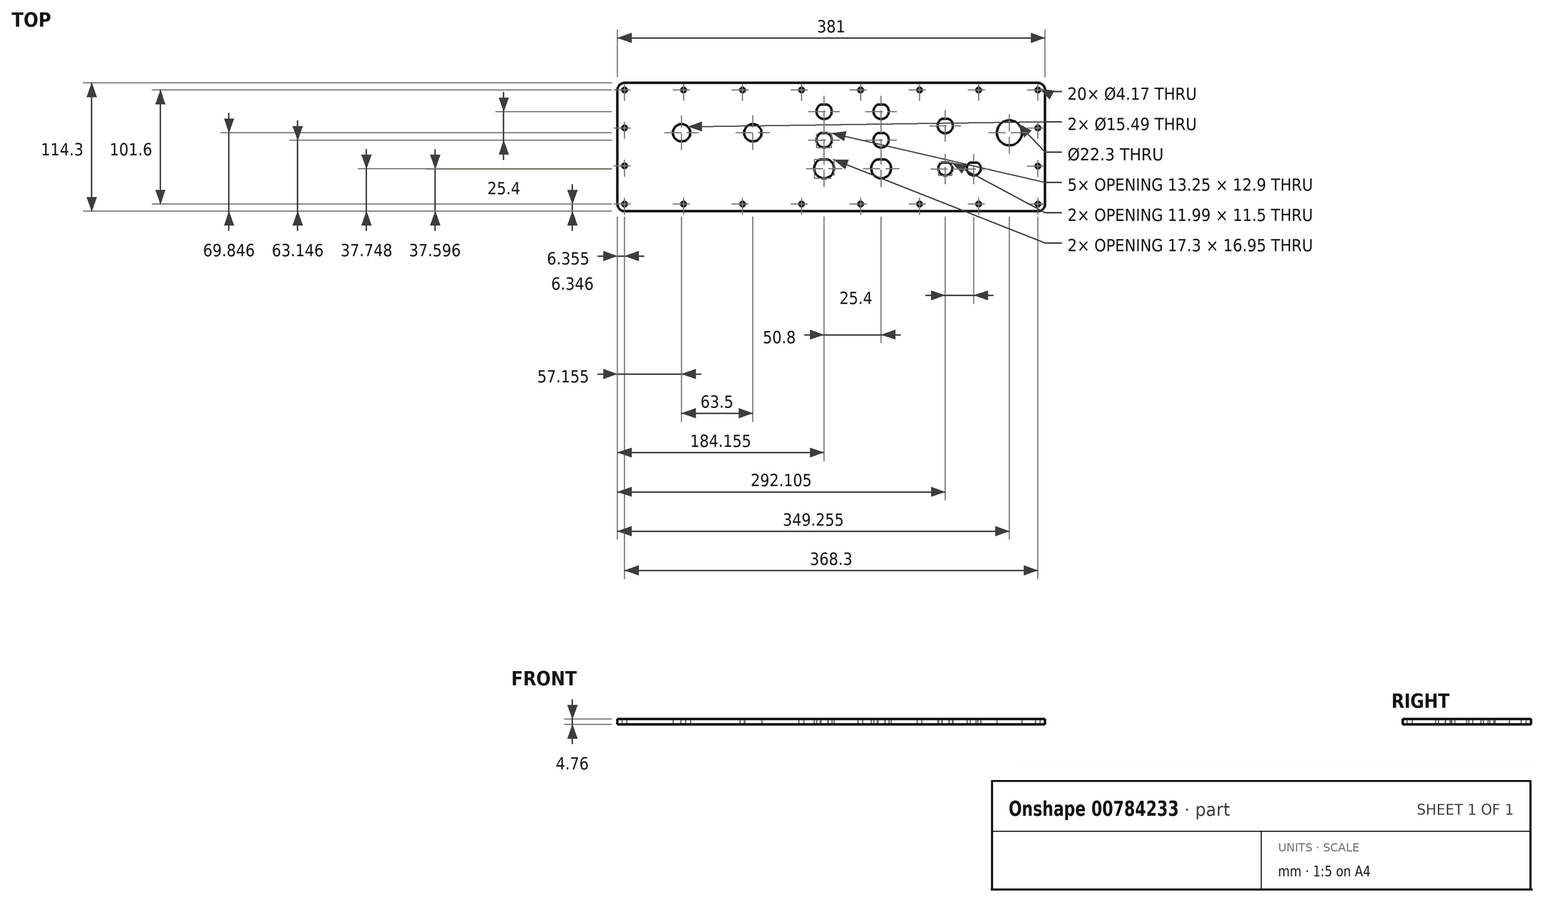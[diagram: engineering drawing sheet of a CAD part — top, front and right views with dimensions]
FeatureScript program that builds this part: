
annotation { "Feature Type Name" : "Feature", "Feature Type Description" : "" }
export const myFeature = defineFeature(function(context is Context, id is Id, definition is map)
    precondition{}
    {
        {
            var Q0;
            Q0=qCreatedBy(makeId("Top.planeOp"),FACE);
            var sketch = newSketch(context, id + "F0", { "sketchPlane" : qUnion([Q0])});
            skLineSegment(sketch, "E0.bottom", {"start": v(-149.25, 72.25) * mm, "end": v(219.05, 72.25) * mm});
            skLineSegment(sketch, "E0.top", {"start": v(-149.25, -42.05) * mm, "end": v(219.05, -42.05) * mm});
            skLineSegment(sketch, "E0.left", {"start": v(-155.6, 65.9) * mm, "end": v(-155.6, -35.7) * mm});
            skLineSegment(sketch, "E0.right", {"start": v(225.4, 65.9) * mm, "end": v(225.4, -35.7) * mm});
            skCircle(sketch, "E1", {"center": v(28.55, -3.95) * mm, "radius": 8.82 * mm});
            skLineSegment(sketch, "E2", {"start": v(25.12, 4.18) * mm, "end": v(31.99, 4.18) * mm});
            skCircle(sketch, "E3.1.0.1", {"center": v(79.35, -3.95) * mm, "radius": 8.82 * mm});
            skLineSegment(sketch, "E3.1.0.4", {"start": v(75.92, 4.18) * mm, "end": v(82.79, 4.18) * mm});
            skLineSegment(sketch, "E3.direction1", {"start": v(28.55, -3.95) * mm, "end": v(79.35, -3.95) * mm, "construction": true});
            skPoint(sketch, "E4", {"position": v(136.5, -3.95) * mm});
            skCircle(sketch, "E5", {"center": v(136.5, -3.95) * mm, "radius": 6.25 * mm});
            skLineSegment(sketch, "E6", {"start": v(133.11, 1.3) * mm, "end": v(139.9, 1.3) * mm});
            skPoint(sketch, "E7", {"position": v(161.9, -3.95) * mm});
            skCircle(sketch, "E8", {"center": v(161.9, -3.95) * mm, "radius": 6.25 * mm});
            skLineSegment(sketch, "E9", {"start": v(158.51, 1.3) * mm, "end": v(165.3, 1.3) * mm});
            skPoint(sketch, "E10", {"position": v(136.5, 34.15) * mm});
            skCircle(sketch, "E11", {"center": v(136.5, 34.15) * mm, "radius": 6.8 * mm});
            skLineSegment(sketch, "E12", {"start": v(139.5, 40.25) * mm, "end": v(139.5, 40.25) * mm});
            skCircle(sketch, "E13", {"center": v(193.65, 27.8) * mm, "radius": 11.15 * mm});
            skCircle(sketch, "E14", {"center": v(-98.45, 27.8) * mm, "radius": 7.75 * mm});
            skCircle(sketch, "E15", {"center": v(-34.95, 27.8) * mm, "radius": 7.75 * mm});
            skLineSegment(sketch, "E16", {"start": v(139.5, 40.25) * mm, "end": v(133.5, 40.25) * mm});
            skCircle(sketch, "E17", {"center": v(28.55, 21.45) * mm, "radius": 6.8 * mm});
            skCircle(sketch, "E18", {"center": v(79.35, 21.45) * mm, "radius": 6.8 * mm});
            skLineSegment(sketch, "E19", {"start": v(25.55, 27.55) * mm, "end": v(31.56, 27.55) * mm});
            skLineSegment(sketch, "E20", {"start": v(76.36, 27.55) * mm, "end": v(82.35, 27.55) * mm});
            skCircle(sketch, "E21", {"center": v(28.55, 46.85) * mm, "radius": 6.8 * mm});
            skCircle(sketch, "E22", {"center": v(79.35, 46.85) * mm, "radius": 6.8 * mm});
            skLineSegment(sketch, "E23", {"start": v(25.55, 52.95) * mm, "end": v(31.56, 52.95) * mm});
            skLineSegment(sketch, "E24", {"start": v(76.36, 52.95) * mm, "end": v(82.35, 52.95) * mm});
            skPoint(sketch, "E25.visualSharp", {"position": v(-155.6, 72.25) * mm});
            skArc(sketch, "E25.filletArc", {"start": v(-149.25, 72.25) * mm, "mid": v(-153.74, 70.39) * mm, "end": v(-155.6, 65.9) * mm});
            skPoint(sketch, "E26.visualSharp", {"position": v(225.4, 72.25) * mm});
            skArc(sketch, "E26.filletArc", {"start": v(225.4, 65.9) * mm, "mid": v(223.54, 70.39) * mm, "end": v(219.05, 72.25) * mm});
            skPoint(sketch, "E27.visualSharp", {"position": v(225.4, -42.05) * mm});
            skArc(sketch, "E27.filletArc", {"start": v(219.05, -42.05) * mm, "mid": v(223.54, -40.2) * mm, "end": v(225.4, -35.7) * mm});
            skPoint(sketch, "E28.visualSharp", {"position": v(-155.6, -42.05) * mm});
            skArc(sketch, "E28.filletArc", {"start": v(-155.6, -35.7) * mm, "mid": v(-153.74, -40.2) * mm, "end": v(-149.25, -42.05) * mm});
            skSolve(sketch);
        }
        {
            var Q0;
            Q0=makeQuery(id+"F0.imprint","IMPRINT",FACE,{"disambiguationData":[TD([[makeQuery(id+"F0.imprint","IMPRINT",EDGE,{"derivedFrom":sQuery(id+"F0.wireOp",EDGE,"E0.bottom")}),-1.0]])]});
            var Q1;
            {var subQ0=sQuery(id+"F0.wireOp",EDGE,"0fb03a76-602c-4fcd-bcda-56a106806c37");Q1=makeQuery(id+"F0.imprint","IMPRINT",FACE,{"disambiguationData":[TD([[makeQuery(id+"F0.imprint","IMPRINT",EDGE,{"derivedFrom":subQ0}),1.0]])]});}
            var Q2;
            {var subQ0=sQuery(id+"F0.wireOp",EDGE,"E3.1.0.3");Q2=makeQuery(id+"F0.imprint","IMPRINT",FACE,{"disambiguationData":[TD([[makeQuery(id+"F0.imprint","IMPRINT",EDGE,{"derivedFrom":subQ0}),1.0]])]});}
            var Q3;
            {var subQ0=sQuery(id+"F0.wireOp",EDGE,"E12");Q3=makeQuery(id+"F0.imprint","IMPRINT",FACE,{"disambiguationData":[TD([[makeQuery(id+"F0.imprint","IMPRINT",EDGE,{"derivedFrom":subQ0}),1.0]])]});}
            var Q4;
            {var subQ0=sQuery(id+"F0.wireOp",EDGE,"fzgxYavN-rOFM-D2aZ-yi2j-a3BjxSNCzOic");Q4=makeQuery(id+"F0.imprint","IMPRINT",FACE,{"disambiguationData":[TD([[makeQuery(id+"F0.imprint","IMPRINT",EDGE,{"derivedFrom":subQ0}),1.0]])]});}
            var Q5;
            {var subQ0=sQuery(id+"F0.wireOp",EDGE,"E3.1.0.5");Q5=makeQuery(id+"F0.imprint","IMPRINT",FACE,{"disambiguationData":[TD([[makeQuery(id+"F0.imprint","IMPRINT",EDGE,{"derivedFrom":subQ0}),1.0]])]});}
            var Q6;
            {var subQ0=sQuery(id+"F0.wireOp",EDGE,"E9");Q6=makeQuery(id+"F0.imprint","IMPRINT",FACE,{"disambiguationData":[TD([[makeQuery(id+"F0.imprint","IMPRINT",EDGE,{"derivedFrom":subQ0}),1.0]])]});}
            var Q7;
            {var subQ0=sQuery(id+"F0.wireOp",EDGE,"E6");Q7=makeQuery(id+"F0.imprint","IMPRINT",FACE,{"disambiguationData":[TD([[makeQuery(id+"F0.imprint","IMPRINT",EDGE,{"derivedFrom":subQ0}),1.0]])]});}
            var Q8;
            {var subQ0=sQuery(id+"F0.wireOp",EDGE,"E2");Q8=makeQuery(id+"F0.imprint","IMPRINT",FACE,{"disambiguationData":[TD([[makeQuery(id+"F0.imprint","IMPRINT",EDGE,{"derivedFrom":subQ0}),1.0]])]});}
            var Q9;
            {var subQ0=sQuery(id+"F0.wireOp",EDGE,"E3.1.0.4");Q9=makeQuery(id+"F0.imprint","IMPRINT",FACE,{"disambiguationData":[TD([[makeQuery(id+"F0.imprint","IMPRINT",EDGE,{"derivedFrom":subQ0}),1.0]])]});}
            var Q10;
            {var subQ0=sQuery(id+"F0.wireOp",EDGE,"E16");Q10=makeQuery(id+"F0.imprint","IMPRINT",FACE,{"disambiguationData":[TD([[makeQuery(id+"F0.imprint","IMPRINT",EDGE,{"derivedFrom":subQ0}),-1.0]])]});}
            var Q11;
            {var subQ0=sQuery(id+"F0.wireOp",EDGE,"E23");Q11=makeQuery(id+"F0.imprint","IMPRINT",FACE,{"disambiguationData":[TD([[makeQuery(id+"F0.imprint","IMPRINT",EDGE,{"derivedFrom":subQ0}),1.0]])]});}
            var Q12;
            {var subQ0=sQuery(id+"F0.wireOp",EDGE,"E24");Q12=makeQuery(id+"F0.imprint","IMPRINT",FACE,{"disambiguationData":[TD([[makeQuery(id+"F0.imprint","IMPRINT",EDGE,{"derivedFrom":subQ0}),1.0]])]});}
            var Q13;
            {var subQ0=sQuery(id+"F0.wireOp",EDGE,"E20");Q13=makeQuery(id+"F0.imprint","IMPRINT",FACE,{"disambiguationData":[TD([[makeQuery(id+"F0.imprint","IMPRINT",EDGE,{"derivedFrom":subQ0}),1.0]])]});}
            var Q14;
            {var subQ0=sQuery(id+"F0.wireOp",EDGE,"E19");Q14=makeQuery(id+"F0.imprint","IMPRINT",FACE,{"disambiguationData":[TD([[makeQuery(id+"F0.imprint","IMPRINT",EDGE,{"derivedFrom":subQ0}),1.0]])]});}
            extrude(context, id + "F1", {"entities" : qUnion([Q0, Q1, Q2, Q3, Q4, Q5, Q6, Q7, Q8, Q9, Q10, Q11, Q12, Q13, Q14]), "depth" : 4.76 * mm, "offsetDistance" : 25.4 * mm});
        }
        {
            var Q0;
            Q0=makeQuery(id+"F1.opExtrude","CAP_FACE",FACE,{"disambiguationData":[OSD([sQuery(id+"F0.wireOp",EDGE,"E0.bottom"),sQuery(id+"F0.wireOp",EDGE,"E0.top"),sQuery(id+"F0.wireOp",EDGE,"E0.left"),sQuery(id+"F0.wireOp",EDGE,"E0.right"),sQuery(id+"F0.wireOp",EDGE,"ucA9xeAH-HVkj-AwQo-CTYJ-HE3rBHppwAKR"),sQuery(id+"F0.wireOp",EDGE,"fzgxYavN-rOFM-D2aZ-yi2j-a3BjxSNCzOic"),sQuery(id+"F0.wireOp",EDGE,"05cf3eeb-7c85-4c40-b4fa-8caa31a27d10"),sQuery(id+"F0.wireOp",EDGE,"0fb03a76-602c-4fcd-bcda-56a106806c37"),sQuery(id+"F0.wireOp",EDGE,"E1"),sQuery(id+"F0.wireOp",EDGE,"E2"),sQuery(id+"F0.wireOp",EDGE,"E3.1.0.0"),sQuery(id+"F0.wireOp",EDGE,"E3.1.0.1"),sQuery(id+"F0.wireOp",EDGE,"E3.1.0.2"),sQuery(id+"F0.wireOp",EDGE,"E3.1.0.3"),sQuery(id+"F0.wireOp",EDGE,"E3.1.0.4"),sQuery(id+"F0.wireOp",EDGE,"E3.1.0.5"),sQuery(id+"F0.wireOp",EDGE,"E5"),sQuery(id+"F0.wireOp",EDGE,"E6"),sQuery(id+"F0.wireOp",EDGE,"E8"),sQuery(id+"F0.wireOp",EDGE,"E9"),sQuery(id+"F0.wireOp",EDGE,"E11"),sQuery(id+"F0.wireOp",EDGE,"E12"),sQuery(id+"F0.wireOp",EDGE,"E13")])],"isStart":false});
            var sketch = newSketch(context, id + "F2", { "sketchPlane" : qUnion([Q0])});
            skPoint(sketch, "E29", {"position": v(-149.25, 65.9) * mm});
            skPoint(sketch, "E30", {"position": v(219.05, 65.9) * mm});
            skPoint(sketch, "E31", {"position": v(219.05, -35.7) * mm});
            skPoint(sketch, "E32", {"position": v(-149.25, -35.7) * mm});
            skLineSegment(sketch, "E33", {"start": v(-149.25, 65.9) * mm, "end": v(-149.25, -35.7) * mm});
            skPoint(sketch, "E34", {"position": v(-149.25, 32.11) * mm});
            skPoint(sketch, "E35", {"position": v(-149.25, -1.67) * mm});
            skLineSegment(sketch, "E36", {"start": v(-149.25, 65.9) * mm, "end": v(219.05, 65.9) * mm});
            skLineSegment(sketch, "E37", {"start": v(219.05, 65.9) * mm, "end": v(219.05, -35.7) * mm});
            skLineSegment(sketch, "E38", {"start": v(219.05, -35.7) * mm, "end": v(-149.25, -35.7) * mm});
            skPoint(sketch, "E39", {"position": v(-96.67, 65.9) * mm});
            skPoint(sketch, "E40", {"position": v(-44.09, 65.9) * mm});
            skPoint(sketch, "E41", {"position": v(8.49, 65.9) * mm});
            skPoint(sketch, "E42", {"position": v(61.07, 65.9) * mm});
            skPoint(sketch, "E43", {"position": v(113.64, 65.9) * mm});
            skPoint(sketch, "E44", {"position": v(166.22, 65.9) * mm});
            skPoint(sketch, "E45", {"position": v(-96.67, -35.7) * mm});
            skPoint(sketch, "E46", {"position": v(-44.09, -35.7) * mm});
            skPoint(sketch, "E47", {"position": v(8.49, -35.7) * mm});
            skPoint(sketch, "E48", {"position": v(61.07, -35.7) * mm});
            skPoint(sketch, "E49", {"position": v(113.64, -35.7) * mm});
            skPoint(sketch, "E50", {"position": v(166.22, -35.7) * mm});
            skPoint(sketch, "E51", {"position": v(219.05, 32.11) * mm});
            skPoint(sketch, "E52", {"position": v(219.05, -1.92) * mm});
            skLineSegment(sketch, "E53.bottom", {"start": v(-142.9, 59.55) * mm, "end": v(212.7, 59.55) * mm});
            skLineSegment(sketch, "E53.top", {"start": v(-142.9, -29.35) * mm, "end": v(212.7, -29.35) * mm});
            skLineSegment(sketch, "E53.left", {"start": v(-142.9, 59.55) * mm, "end": v(-142.9, -29.35) * mm});
            skLineSegment(sketch, "E53.right", {"start": v(212.7, 59.55) * mm, "end": v(212.7, -29.35) * mm});
            skSolve(sketch);
        }
        {
            var Q0;
            Q0=sQuery(id+"F2.wireOp",VERTEX,"E29");
            var Q1;
            Q1=sQuery(id+"F2.wireOp",VERTEX,"E32");
            var Q2;
            Q2=sQuery(id+"F2.wireOp",VERTEX,"E30");
            var Q3;
            Q3=sQuery(id+"F2.wireOp",VERTEX,"E31");
            var Q4;
            Q4=sQuery(id+"F2.wireOp",VERTEX,"E39");
            var Q5;
            Q5=sQuery(id+"F2.wireOp",VERTEX,"E43");
            var Q6;
            Q6=sQuery(id+"F2.wireOp",VERTEX,"E42");
            var Q7;
            Q7=sQuery(id+"F2.wireOp",VERTEX,"E44");
            var Q8;
            Q8=sQuery(id+"F2.wireOp",VERTEX,"E41");
            var Q9;
            Q9=sQuery(id+"F2.wireOp",VERTEX,"E40");
            var Q10;
            Q10=sQuery(id+"F2.wireOp",VERTEX,"E35");
            var Q11;
            Q11=sQuery(id+"F2.wireOp",VERTEX,"6f18e72d-e5f8-4749-99b7-cfa222df317b");
            var Q12;
            Q12=sQuery(id+"F2.wireOp",VERTEX,"E34");
            var Q13;
            Q13=sQuery(id+"F2.wireOp",VERTEX,"E48");
            var Q14;
            Q14=sQuery(id+"F2.wireOp",VERTEX,"E50");
            var Q15;
            Q15=sQuery(id+"F2.wireOp",VERTEX,"E45");
            var Q16;
            Q16=sQuery(id+"F2.wireOp",VERTEX,"E46");
            var Q17;
            Q17=sQuery(id+"F2.wireOp",VERTEX,"E49");
            var Q18;
            Q18=sQuery(id+"F2.wireOp",VERTEX,"E47");
            var Q19;
            Q19=sQuery(id+"F2.wireOp",VERTEX,"26664f4a-105a-4f21-ac9c-66ad29a12fca");
            var Q20;
            Q20=sQuery(id+"F2.wireOp",VERTEX,"E52");
            var Q21;
            Q21=sQuery(id+"F2.wireOp",VERTEX,"E51");
            var Q22;
            Q22=makeQuery(id+"F1.opExtrude","SWEPT_BODY",BODY,{"disambiguationData":[OSD([sQuery(id+"F0.wireOp",EDGE,"E0.bottom"),sQuery(id+"F0.wireOp",EDGE,"E0.top"),sQuery(id+"F0.wireOp",EDGE,"E0.left"),sQuery(id+"F0.wireOp",EDGE,"E0.right"),sQuery(id+"F0.wireOp",EDGE,"ucA9xeAH-HVkj-AwQo-CTYJ-HE3rBHppwAKR"),sQuery(id+"F0.wireOp",EDGE,"fzgxYavN-rOFM-D2aZ-yi2j-a3BjxSNCzOic"),sQuery(id+"F0.wireOp",EDGE,"05cf3eeb-7c85-4c40-b4fa-8caa31a27d10"),sQuery(id+"F0.wireOp",EDGE,"0fb03a76-602c-4fcd-bcda-56a106806c37"),sQuery(id+"F0.wireOp",EDGE,"E1"),sQuery(id+"F0.wireOp",EDGE,"E2"),sQuery(id+"F0.wireOp",EDGE,"E3.1.0.0"),sQuery(id+"F0.wireOp",EDGE,"E3.1.0.1"),sQuery(id+"F0.wireOp",EDGE,"E3.1.0.2"),sQuery(id+"F0.wireOp",EDGE,"E3.1.0.3"),sQuery(id+"F0.wireOp",EDGE,"E3.1.0.4"),sQuery(id+"F0.wireOp",EDGE,"E3.1.0.5"),sQuery(id+"F0.wireOp",EDGE,"E5"),sQuery(id+"F0.wireOp",EDGE,"E6"),sQuery(id+"F0.wireOp",EDGE,"E8"),sQuery(id+"F0.wireOp",EDGE,"E9"),sQuery(id+"F0.wireOp",EDGE,"E11"),sQuery(id+"F0.wireOp",EDGE,"E12"),sQuery(id+"F0.wireOp",EDGE,"E13"),sQuery(id+"F0.wireOp",EDGE,"E14"),sQuery(id+"F0.wireOp",EDGE,"E15")])]});
            hole(context, id + "F3", {"style" : HoleStyle.SIMPLE, "endStyle" : HoleEndStyle.THROUGH, "holeDiameter" : 4.17 * mm, "majorDiameter" : 6.35 * mm, "isTappedThrough" : true, "tappedDepth" : 12.7 * mm, "tapClearance" : 3, "locations" : qUnion([Q0, Q1, Q2, Q3, Q4, Q5, Q6, Q7, Q8, Q9, Q10, Q11, Q12, Q13, Q14, Q15, Q16, Q17, Q18, Q19, Q20, Q21]), "scope" : qUnion([Q22])});
        }
    });
